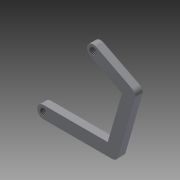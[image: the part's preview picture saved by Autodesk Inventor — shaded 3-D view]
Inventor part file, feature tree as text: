
AUTODESK INVENTOR PART (.ipt)
format: ipt  version: 2015 SP2 (Build 190223200, 223)  size: 101,888 bytes
history: native  units: mm
features: extrude x3, sketch x3, thread x2
ambient origin geometry x8: Origin, YZ Plane, XZ Plane, XY Plane, X Axis, Y Axis, Z Axis, Center Point
bodies: Solid1 (feature_tree)
feature tree (8):
  extrude  "Extrusion1"  Depth=5.0mm
  extrude  "Extrusion2"  Depth=3.0mm
  thread  "Thread2"  [1 undecoded]
  extrude  "Extrusion3"  Depth=10.0mm TaperAngle=0.0deg
  thread  "Thread3"  [1 undecoded]
  sketch  "Sketch1"  dims[d0=5.0mm d1=5.0mm]
  sketch  "Sketch2"  dims[d2=5.0mm d3=5.0mm d4=3.0mm d5=0.0mm]
  sketch  "Sketch3"  dims[d6=2.8mm d7=8.0mm d8=0.0mm d11=10.0mm d12=0.0mm d13=3.0mm d14=10.0mm d15=0.0mm d16=10.0mm d17=0.0mm]
note: 2 required parameter values undecoded (feature->parameter linkage not recoverable at this tier; creation-order binding heuristic only, values carry confidence <= 0.55)
